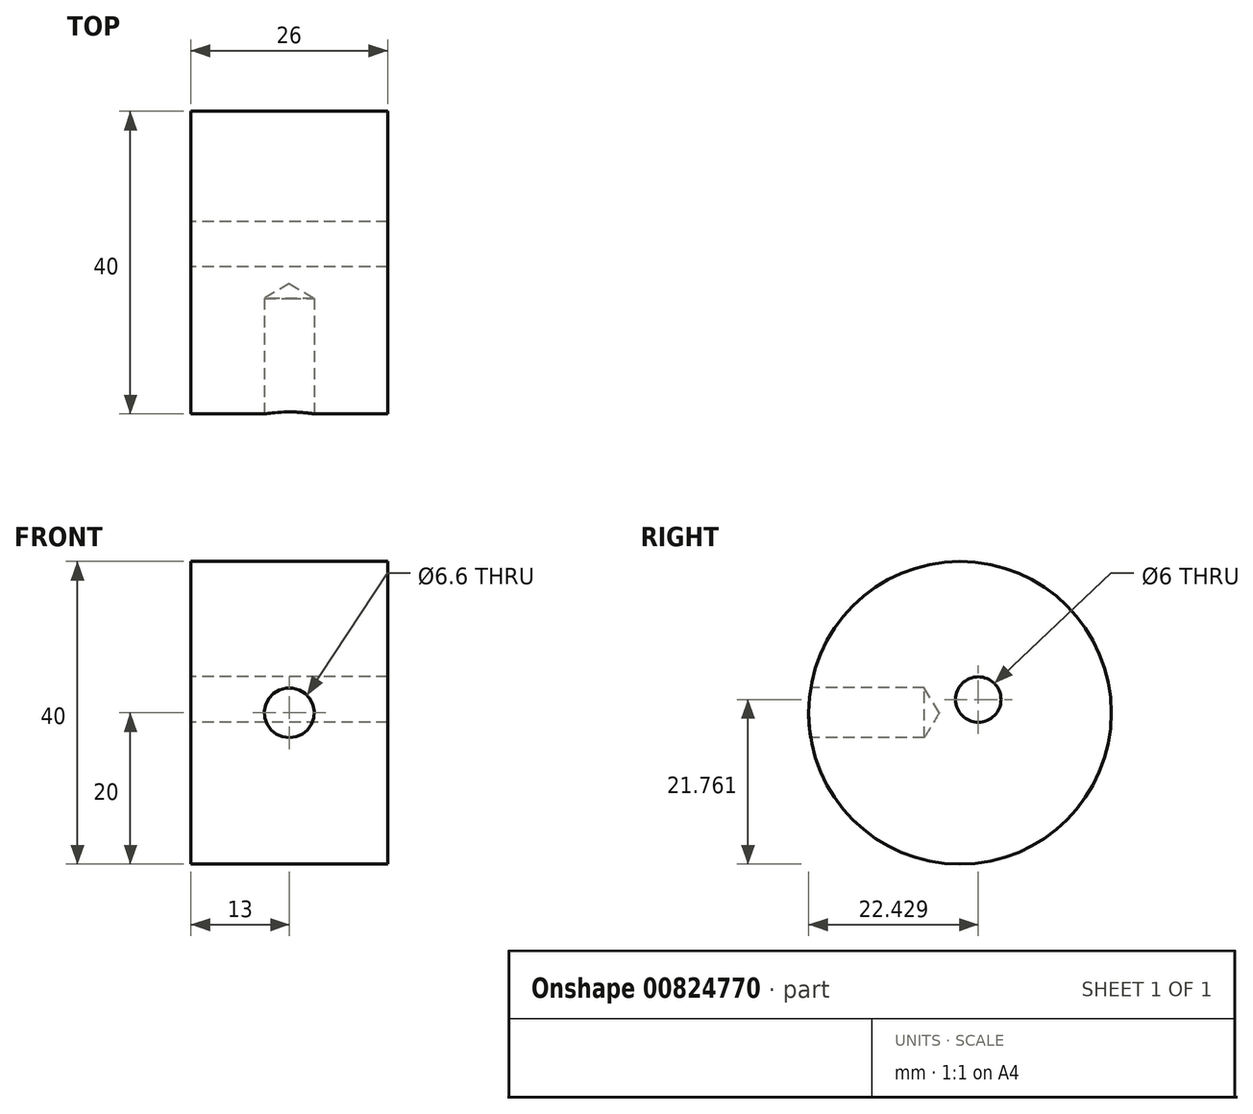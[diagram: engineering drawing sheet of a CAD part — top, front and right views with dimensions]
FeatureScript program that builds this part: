
annotation { "Feature Type Name" : "Feature", "Feature Type Description" : "" }
export const myFeature = defineFeature(function(context is Context, id is Id, definition is map)
    precondition{}
    {
        {
            var Q0;
            Q0=qCreatedBy(makeId("Right.planeOp"),FACE);
            var sketch = newSketch(context, id + "F0", { "sketchPlane" : qUnion([Q0])});
            skCircle(sketch, "E0", {"center": v(0, 0) * mm, "radius": 20 * mm});
            skLineSegment(sketch, "E1", {"start": v(0, 0) * mm, "end": v(3, 0) * mm});
            skLineSegment(sketch, "E2", {"start": v(0, 0) * mm, "end": v(-20, 0) * mm});
            skLineSegment(sketch, "E3", {"start": v(0, 0) * mm, "end": v(2.48, -1.69) * mm});
            skLineSegment(sketch, "E4", {"start": v(0, 0) * mm, "end": v(2.43, 1.76) * mm});
            skCircle(sketch, "E5", {"center": v(2.43, 1.76) * mm, "radius": 3 * mm});
            skSolve(sketch);
        }
        {
            var Q0;
            Q0=makeQuery(id+"F0.imprint","IMPRINT",FACE,{"disambiguationData":[TD([[makeQuery(id+"F0.imprint","IMPRINT",EDGE,{"derivedFrom":sQuery(id+"F0.wireOp",EDGE,"E0")}),1.0]])]});
            extrude(context, id + "F1", {"entities" : qUnion([Q0]), "depth" : 26 * mm, "offsetDistance" : 25 * mm});
        }
        {
            var Q0;
            Q0=sQuery(id+"F0.wireOp",VERTEX,"E2.end");
            var Q1;
            Q1=sQuery(id+"F0.wireOp",EDGE,"E2");
            cPlane(context, id + "F2", {"entities" : qUnion([Q0, Q1]), "cplaneType" : CPlaneType.CURVE_POINT, "offset" : 25 * mm, "width" : 150 * mm, "height" : 150 * mm});
        }
        {
            var Q0;
            Q0=qCreatedBy(id+"F2.planeOp",FACE);
            var sketch = newSketch(context, id + "F3", { "sketchPlane" : qUnion([Q0])});
            skPoint(sketch, "E6", {"position": v(13, 0) * mm});
            skSolve(sketch);
        }
        {
            var Q0;
            Q0=sQuery(id+"F3.wireOp",VERTEX,"E6");
            var Q1;
            Q1=makeQuery(id+"F1.opExtrude","SWEPT_BODY",BODY,{"disambiguationData":[OSD([sQuery(id+"F0.wireOp",EDGE,"E0"),sQuery(id+"F0.wireOp",EDGE,"y9aqhLCG-ZLdv-dYda-rCv1-GXRxGbeIF3Ql")])]});
            hole(context, id + "F4", {"style" : HoleStyle.SIMPLE, "endStyle" : HoleEndStyle.BLIND, "standardTappedOrClearance" : lookupTablePath({ "standard" : "ISO", "fit" : "Normal", "size" : "M6", "type" : "Clearance" }), "standardBlindInLast" : lookupTablePath({ "fit" : "Standard", "standard" : "ISO", "size" : "M6", "type" : "Clearance" }), "holeDiameter" : 6.6 * mm, "majorDiameter" : 6 * mm, "holeDepth" : 15 * mm, "isTappedThrough" : true, "tappedDepth" : 12 * mm, "tapClearance" : 3, "locations" : qUnion([Q0]), "scope" : qUnion([Q1])});
        }
    });
